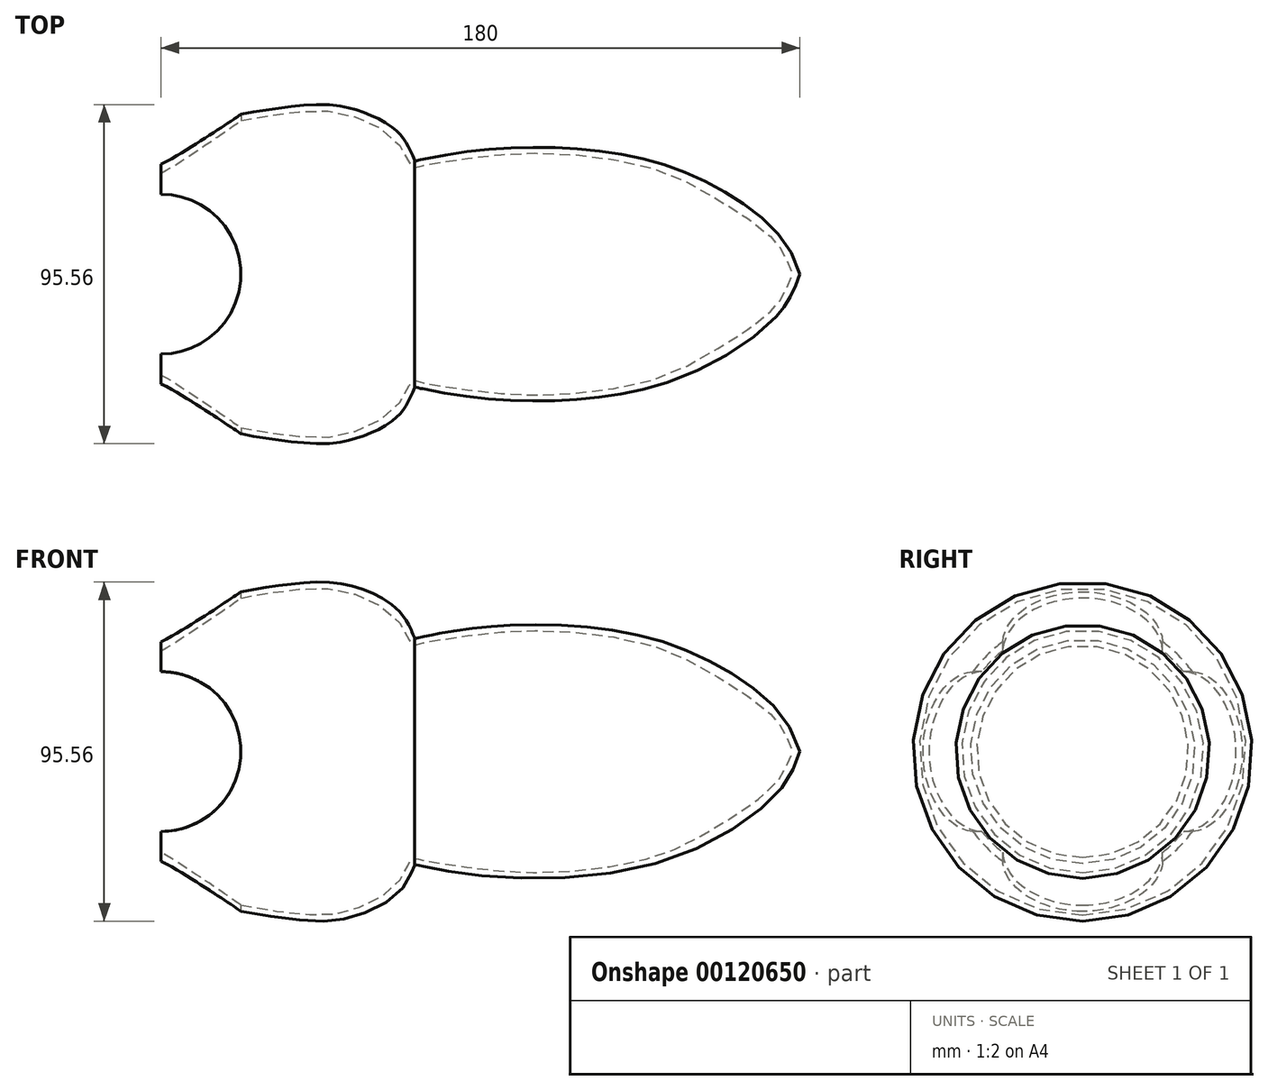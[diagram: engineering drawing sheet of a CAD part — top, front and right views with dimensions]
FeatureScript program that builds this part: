
annotation { "Feature Type Name" : "Feature", "Feature Type Description" : "" }
export const myFeature = defineFeature(function(context is Context, id is Id, definition is map)
    precondition{}
    {
        {
            var Q0;
            Q0=qCreatedBy(makeId("Front.planeOp"),FACE);
            var sketch = newSketch(context, id + "F0", { "sketchPlane" : qUnion([Q0])});
            skLineSegment(sketch, "E0.0", {"start": v(-18.15, -28) * mm, "end": v(-7.75, -28) * mm});
            skLineSegment(sketch, "E0.1", {"start": v(-29.5, -28) * mm, "end": v(-25.65, -28) * mm});
            skArc(sketch, "E0.2", {"start": v(-32.5, -25) * mm, "mid": v(-31.62, -27.12) * mm, "end": v(-29.5, -28) * mm});
            skLineSegment(sketch, "E0.3", {"start": v(-32.5, 25) * mm, "end": v(-32.5, -25) * mm});
            skCircle(sketch, "E0.4", {"center": v(-29, -24.5) * mm, "radius": 1.38 * mm});
            skArc(sketch, "E0.5", {"start": v(-29.5, 28) * mm, "mid": v(-31.62, 27.12) * mm, "end": v(-32.5, 25) * mm});
            skLineSegment(sketch, "E0.6", {"start": v(49.5, 28) * mm, "end": v(-29.5, 28) * mm});
            skCircle(sketch, "E0.7", {"center": v(-29, 24.5) * mm, "radius": 1.38 * mm});
            skCircle(sketch, "E0.8", {"center": v(29, 24.5) * mm, "radius": 1.38 * mm});
            skCircle(sketch, "E0.9", {"center": v(29, -24.5) * mm, "radius": 1.38 * mm});
            skLineSegment(sketch, "E0.10", {"start": v(24.5, -28) * mm, "end": v(49.5, -28) * mm});
            skArc(sketch, "E0.11", {"start": v(49.5, -28) * mm, "mid": v(51.37, -27.34) * mm, "end": v(52.43, -25.66) * mm});
            skLineSegment(sketch, "E0.12", {"start": v(52.5, -9.78) * mm, "end": v(52.5, -5.5) * mm});
            skLineSegment(sketch, "E0.13", {"start": v(52.5, 7.5) * mm, "end": v(52.5, 12.5) * mm});
            skArc(sketch, "E0.14", {"start": v(52.46, 25.5) * mm, "mid": v(51.44, 27.3) * mm, "end": v(49.5, 28) * mm});
            skLineSegment(sketch, "E0.15", {"start": v(6.75, -28) * mm, "end": v(17.5, -28) * mm});
            skLineSegment(sketch, "E1", {"start": v(52.46, 25.5) * mm, "end": v(52.5, 12.5) * mm, "construction": true});
            skLineSegment(sketch, "E2", {"start": v(52.5, 7.5) * mm, "end": v(52.5, -5.5) * mm, "construction": true});
            skLineSegment(sketch, "E3", {"start": v(52.5, -9.78) * mm, "end": v(52.43, -25.66) * mm, "construction": true});
            skLineSegment(sketch, "E4", {"start": v(24.5, -28) * mm, "end": v(17.5, -28) * mm, "construction": true});
            skLineSegment(sketch, "E5", {"start": v(6.75, -28) * mm, "end": v(-7.75, -28) * mm, "construction": true});
            skLineSegment(sketch, "E6", {"start": v(-18.15, -28) * mm, "end": v(-25.65, -28) * mm, "construction": true});
            skLineSegment(sketch, "E7", {"start": v(-29, 24.5) * mm, "end": v(29, -24.5) * mm, "construction": true});
            skLineSegment(sketch, "E8", {"start": v(29, 24.5) * mm, "end": v(-29, -24.5) * mm, "construction": true});
            skLineSegment(sketch, "E9", {"start": v(-29, 24.5) * mm, "end": v(-29, -24.5) * mm, "construction": true});
            skLineSegment(sketch, "E10", {"start": v(-29, -24.5) * mm, "end": v(29, -24.5) * mm, "construction": true});
            skLineSegment(sketch, "E11", {"start": v(29, -24.5) * mm, "end": v(29, 24.5) * mm, "construction": true});
            skLineSegment(sketch, "E12", {"start": v(29, 24.5) * mm, "end": v(-29, 24.5) * mm, "construction": true});
            skPoint(sketch, "E13", {"position": v(0, 0) * mm});
            skLineSegment(sketch, "E14", {"start": v(-90.89, 0) * mm, "end": v(89.11, 0) * mm});
            skFitSpline(sketch, "E15", {"points": [v(-90.89, 0) * mm, v(-90.89, -38.26) * mm], "startDerivative": vector(0, -38.26) * mm, "endDerivative": vector(0, -38.26) * mm});
            skFitSpline(sketch, "E16", {"points": [v(89.11, 0) * mm, v(83.45, -10.93) * mm, v(48.7, -31.48) * mm, v(-4.37, -34.53) * mm, v(-18.5, -32.06) * mm, v(-18.96, -31.91) * mm, v(-19.45, -31.6) * mm, v(-19.5, -32.13) * mm, v(-19.8, -32.9) * mm, v(-23.52, -39.33) * mm, v(-36.68, -46.51) * mm, v(-50.06, -47.62) * mm, v(-73.8, -43.89) * mm, v(-84.32, -40.77) * mm, v(-90.89, -38.26) * mm], "startDerivative": vector(-44.84, -134.87) * mm, "endDerivative": vector(-109.09, 43.01) * mm});
            skPoint(sketch, "E17", {"position": v(-90.89, -36.26) * mm});
            skLineSegment(sketch, "E18", {"start": v(-90.89, -36.26) * mm, "end": v(-90.89, -38.26) * mm});
            skFitSpline(sketch, "E19", {"points": [v(-90.89, -36.26) * mm, v(-83.87, -39.09) * mm, v(-73.4, -42.23) * mm, v(-49.8, -45.91) * mm, v(-37.3, -44.68) * mm, v(-25.2, -38.15) * mm, v(-21.67, -32.7) * mm, v(-20.57, -30.63) * mm, v(-20.16, -29.88) * mm, v(-19.26, -30.05) * mm, v(-17.64, -30.52) * mm, v(-4.1, -32.7) * mm, v(19.02, -34.03) * mm, v(47.69, -29.82) * mm, v(63.67, -22.4) * mm, v(81.9, -9.57) * mm, v(85.92, -2.96) * mm, v(87.11, 0) * mm], "startDerivative": vector(132.54, -55.78) * mm, "endDerivative": vector(23.1, 78.9) * mm});
            skLineSegment(sketch, "E20", {"start": v(87.11, 0) * mm, "end": v(89.11, 0) * mm});
            skLineSegment(sketch, "E21", {"start": v(0, 0) * mm, "end": v(-102.3, 0) * mm, "construction": true});
            skCircle(sketch, "E22", {"center": v(-90.89, 0) * mm, "radius": 22.5 * mm});
            skSolve(sketch);
        }
        {
            var Q0;
            Q0=makeQuery(id+"F0.imprint","IMPRINT",FACE,{"disambiguationData":[TD([[makeQuery(id+"F0.imprint","IMPRINT",EDGE,{"derivedFrom":sQuery(id+"F0.wireOp",EDGE,"E16")}),-1.0]])]});
            var Q1;
            Q1=sQuery(id+"F0.wireOp",EDGE,"E21");
            revolve(context, id + "F1", {"entities" : qUnion([Q0]), "axis" : qUnion([Q1]), "revolveType" : RevolveType.FULL});
        }
        {
            var Q0;
            {var subQ0=sQuery(id+"F0.wireOp",EDGE,"E15");var subQ1=sQuery(id+"F0.wireOp",EDGE,"E14");var subQ2=makeQuery(id+"F0.imprint","INTERSECT",VERTEX,{"derivedFrom":[subQ1,subQ0]});Q0=makeQuery(id+"F0.imprint","IMPRINT",FACE,{"disambiguationData":[TD([[makeQuery(id+"F0.imprint","IMPRINT",EDGE,{"disambiguationData":[TD([[subQ2,-1.0]])],"derivedFrom":subQ1}),1.0]])]});}
            var Q1;
            {var subQ0=sQuery(id+"F0.wireOp",EDGE,"E15");var subQ1=sQuery(id+"F0.wireOp",EDGE,"E14");var subQ2=makeQuery(id+"F0.imprint","INTERSECT",VERTEX,{"derivedFrom":[subQ1,subQ0]});Q1=makeQuery(id+"F0.imprint","IMPRINT",FACE,{"disambiguationData":[TD([[makeQuery(id+"F0.imprint","IMPRINT",EDGE,{"disambiguationData":[TD([[subQ2,-1.0]])],"derivedFrom":subQ1}),-1.0]])]});}
            extrude(context, id + "F2", {"entities" : qUnion([Q0, Q1]), "operationType" : NewBodyOperationType.REMOVE, "oppositeDirection" : true, "depth" : 100 * mm, "hasSecondDirection" : true, "secondDirectionOppositeDirection" : false, "secondDirectionDepth" : 100 * mm});
        }
        {
            var Q0;
            Q0=qCreatedBy(makeId("Top.planeOp"),FACE);
            var sketch = newSketch(context, id + "F3", { "sketchPlane" : qUnion([Q0])});
            skLineSegment(sketch, "E23.0", {"start": v(-90.89, -30.94) * mm, "end": v(-90.89, 30.94) * mm});
            skLineSegment(sketch, "E24", {"start": v(0, 0) * mm, "end": v(-120, 0) * mm, "construction": true});
            skPoint(sketch, "E25", {"position": v(-90.89, 0) * mm});
            skCircle(sketch, "E26", {"center": v(-90.89, 0) * mm, "radius": 22.5 * mm});
            skSolve(sketch);
        }
        {
            var Q0;
            {var subQ0=sQuery(id+"F3.wireOp",EDGE,"E26");var subQ1=sQuery(id+"F3.wireOp",EDGE,"E23.0");var subQ2=makeQuery(id+"F3.imprint","INTERSECT",VERTEX,{"disambiguationData":[OD(0.0)],"derivedFrom":[subQ1,subQ0]});Q0=makeQuery(id+"F3.imprint","IMPRINT",FACE,{"disambiguationData":[TD([[makeQuery(id+"F3.imprint","IMPRINT",EDGE,{"disambiguationData":[TD([[subQ2,-1.0]])],"derivedFrom":subQ1}),1.0]])]});}
            var Q1;
            {var subQ0=sQuery(id+"F3.wireOp",EDGE,"E26");var subQ1=sQuery(id+"F3.wireOp",EDGE,"E23.0");var subQ2=makeQuery(id+"F3.imprint","INTERSECT",VERTEX,{"disambiguationData":[OD(0.0)],"derivedFrom":[subQ1,subQ0]});Q1=makeQuery(id+"F3.imprint","IMPRINT",FACE,{"disambiguationData":[TD([[makeQuery(id+"F3.imprint","IMPRINT",EDGE,{"disambiguationData":[TD([[subQ2,-1.0]])],"derivedFrom":subQ1}),-1.0]])]});}
            extrude(context, id + "F4", {"entities" : qUnion([Q0, Q1]), "operationType" : NewBodyOperationType.REMOVE, "oppositeDirection" : true, "depth" : 100 * mm, "hasSecondDirection" : true, "secondDirectionOppositeDirection" : false, "secondDirectionDepth" : 100 * mm});
        }
    });
